# Revit family: Table-LAMMHULTS-ATTACH-Rectangular
name_source: partatom
category: Furniture
revit_build: Autodesk Revit 2014 (Build: 20140709_2115(x64)
units: mm (PartAtom-declared; Revit-internal decimal feet)

## types (11) — shared parameters
Assembly Code = E2020
Description = *Please enter mtrl description here for use in mto*
Foot Material = Plastic - Black
Frame Material = Metal - Aluminium - Matte
Keynote = 46.B
Legs Material = Metal - Aluminium - Matte
Manufacturer = LAMMHULTS
Model = ATTACH
Table Top Material = Laminate - High Pressure - White/Grey
URL = www.lammhults.se

## per-type parameters (varying)
| type | Frame Positioning | Frame inset | Leg Positioning | Long Frame (10) | Short Frame (310) | Six Leg | Table Top Length | Table Top Width |
| 90x210 Laminate broken white | 262.5 mm | 10 mm  [stored 0.0328084 ft] | 50 mm  [stored 0.164042 ft] | Yes | No | No | 2100 mm | 900 mm |
| 90x290 Laminate broken white | 262.5 mm | 10 mm  [stored 0.0328084 ft] | 50 mm  [stored 0.164042 ft] | Yes | No | No | 2900 mm | 900 mm |
| 90x420 Laminate broken white | 262.5 mm | 310 mm | 290 mm | No | Yes | No | 4200 mm | 900 mm |
| 90x580 Laminate broken white | 262.5 mm | 10 mm  [stored 0.0328084 ft] | 50 mm  [stored 0.164042 ft] | Yes | No | Yes | 5800 mm | 900 mm |
| 120x240 Laminate broken white | 262.5 mm | 10 mm  [stored 0.0328084 ft] | 50 mm  [stored 0.164042 ft] | Yes | No | No | 2400 mm | 1200 mm  [stored 3.93701 ft] |
| 120x290 Laminate broken white | 262.5 mm | 10 mm  [stored 0.0328084 ft] | 50 mm  [stored 0.164042 ft] | Yes | No | No | 2900 mm | 1200 mm  [stored 3.93701 ft] |
| 120x580 Laminate broken white | 262.5 mm | 10 mm  [stored 0.0328084 ft] | 50 mm  [stored 0.164042 ft] | Yes | No | Yes | 5800 mm | 1200 mm  [stored 3.93701 ft] |
| 150x240 Laminate broken white | 337.5 mm | 10 mm  [stored 0.0328084 ft] | 50 mm  [stored 0.164042 ft] | Yes | No | No | 2400 mm | 1500 mm |
| 150x480 Laminate broken white | 337.5 mm | 310 mm | 590 mm | No | Yes | No | 4800 mm | 1500 mm |
| 200x400 Laminate broken white | 562.5 mm | 310 mm | 190 mm | No | Yes | No | 4000 mm  [stored 13.1234 ft] | 2000 mm |
| 200x600 Laminate broken white | 562.5 mm | 10 mm  [stored 0.0328084 ft] | 50 mm  [stored 0.164042 ft] | Yes | No | Yes | 6000 mm | 2000 mm |

note: [stored X ft] marks values corroborated as IEEE doubles in the binary element streams (Revit-internal decimal feet)

## geometry (parser evidence)
native form markers: Blend x10, Sweep x8
no freeform markers — native parametric forms only
